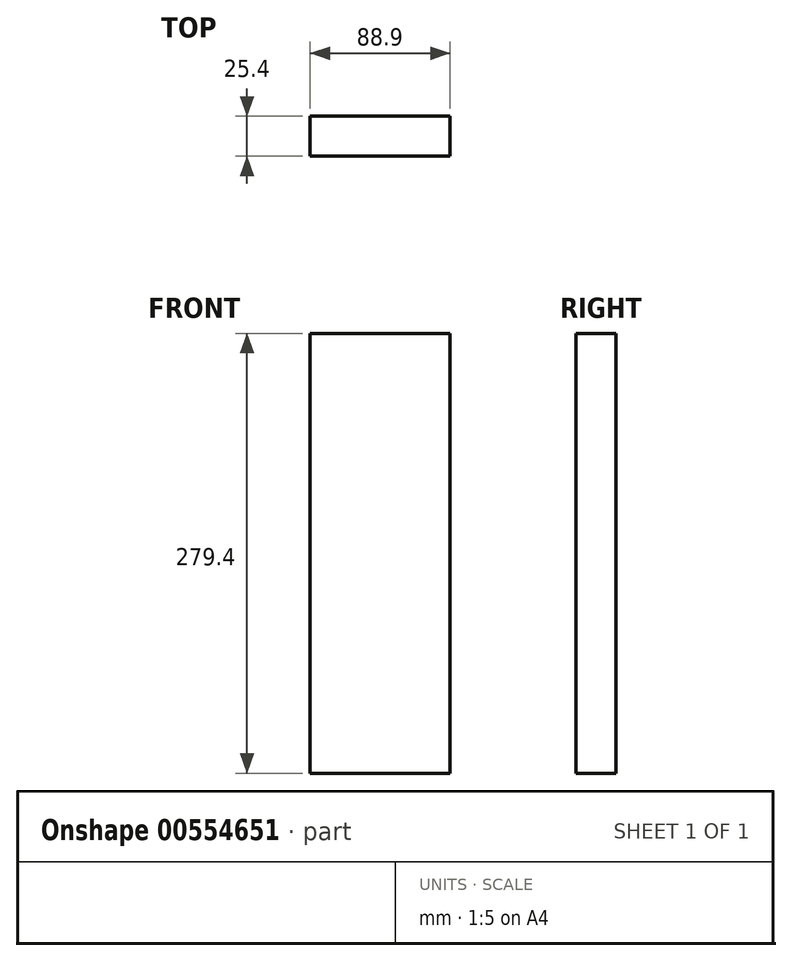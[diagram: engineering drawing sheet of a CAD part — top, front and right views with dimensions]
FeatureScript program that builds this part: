
annotation { "Feature Type Name" : "Feature", "Feature Type Description" : "" }
export const myFeature = defineFeature(function(context is Context, id is Id, definition is map)
    precondition{}
    {
        {
            var Q0;
            Q0=qCreatedBy(makeId("Front.planeOp"),FACE);
            var sketch = newSketch(context, id + "F0", { "sketchPlane" : qUnion([Q0])});
            skLineSegment(sketch, "E0", {"start": v(-178.89, 279.4) * mm, "end": v(-178.89, 0) * mm});
            skLineSegment(sketch, "E1", {"start": v(-178.89, 0) * mm, "end": v(-89.99, 0) * mm});
            skLineSegment(sketch, "E2", {"start": v(-89.99, 0) * mm, "end": v(-89.99, 279.4) * mm});
            skLineSegment(sketch, "E3", {"start": v(-89.99, 279.4) * mm, "end": v(-178.89, 279.4) * mm});
            skSolve(sketch);
        }
        {
            var Q0;
            Q0 = qSketchRegion(id + "F0", true);
            extrude(context, id + "F1", {"entities" : qUnion([Q0]), "depth" : 25.4 * mm, "offsetDistance" : 25.4 * mm});
        }
    });
